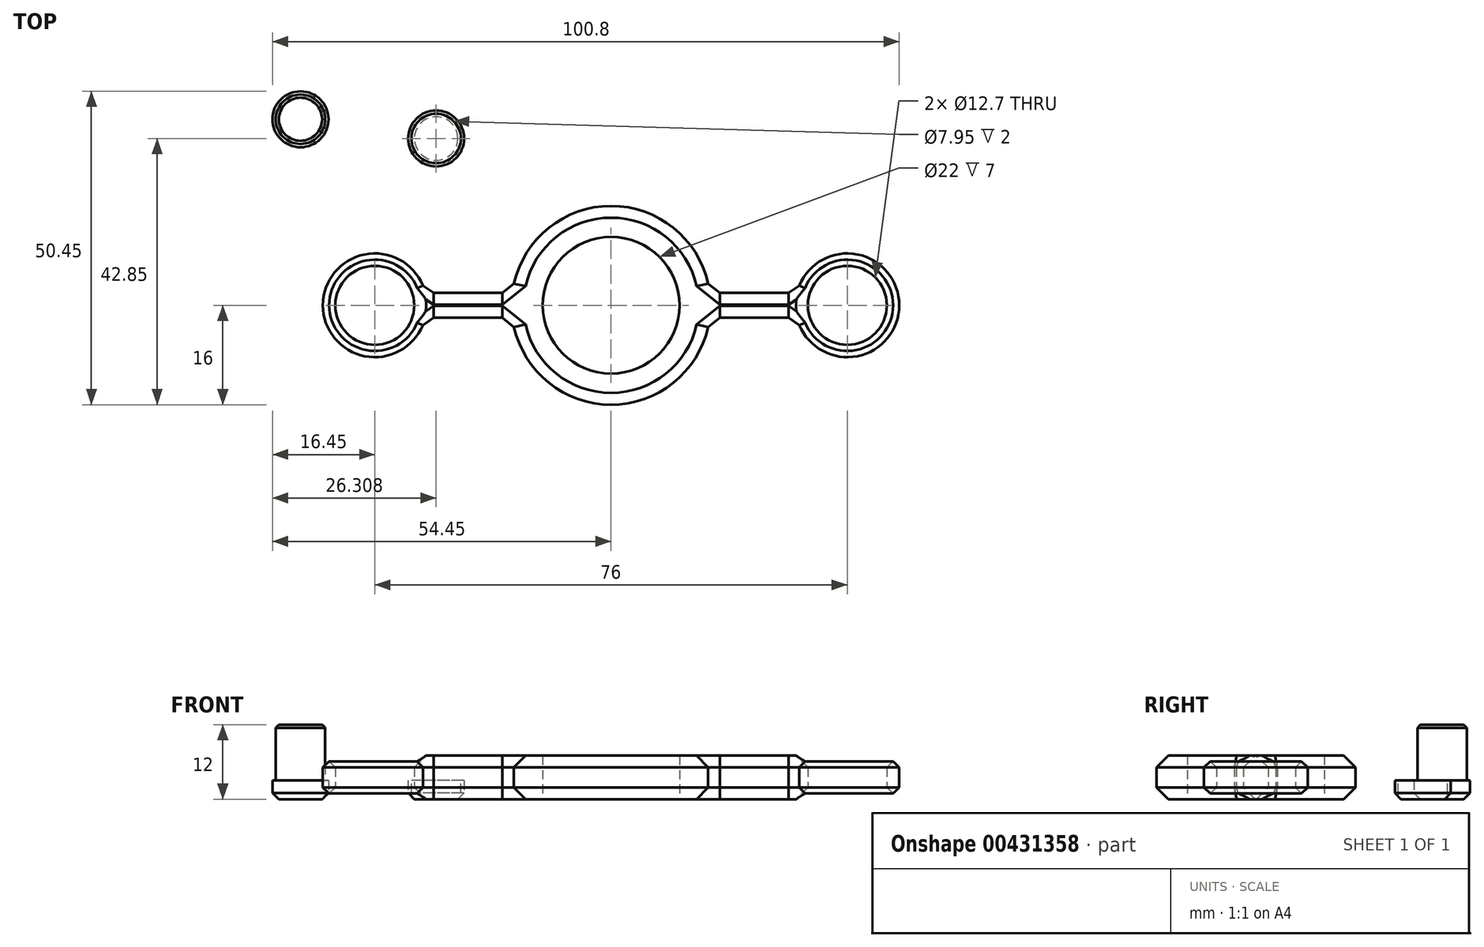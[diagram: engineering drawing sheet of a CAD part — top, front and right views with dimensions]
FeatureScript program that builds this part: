
annotation { "Feature Type Name" : "Feature", "Feature Type Description" : "" }
export const myFeature = defineFeature(function(context is Context, id is Id, definition is map)
    precondition{}
    {
        {
            var Q0;
            Q0=qCreatedBy(makeId("Top.planeOp"),FACE);
            var sketch = newSketch(context, id + "F0", { "sketchPlane" : qUnion([Q0])});
            skCircle(sketch, "E0", {"center": v(0, 0) * mm, "radius": 11 * mm});
            skArc(sketch, "E1.0", {"start": v(15.87, 2) * mm, "mid": v(0, 16) * mm, "end": v(-15.87, 2) * mm});
            skCircle(sketch, "E2", {"center": v(38, 0) * mm, "radius": 6.35 * mm});
            skArc(sketch, "E3.0", {"start": v(29.9, -2) * mm, "mid": v(46.35, 0) * mm, "end": v(29.9, 2) * mm});
            skLineSegment(sketch, "E4.trimOffspring", {"start": v(15.87, 2) * mm, "end": v(29.9, 2) * mm});
            skLineSegment(sketch, "E5.trimOffspring", {"start": v(15.87, -2) * mm, "end": v(29.9, -2) * mm});
            skArc(sketch, "E6.MirrorCS", {"start": v(-29.9, -2) * mm, "mid": v(-46.35, 0) * mm, "end": v(-29.9, 2) * mm});
            skLineSegment(sketch, "E7.MirrorCS", {"start": v(-15.87, 2) * mm, "end": v(-29.9, 2) * mm});
            skLineSegment(sketch, "E8.MirrorCS", {"start": v(-15.87, -2) * mm, "end": v(-29.9, -2) * mm});
            skCircle(sketch, "E9.MirrorC", {"center": v(-38, 0) * mm, "radius": 6.35 * mm});
            skArc(sketch, "E10.MirrorCS", {"start": v(-15.87, 2) * mm, "mid": v(0, 16) * mm, "end": v(15.87, 2) * mm});
            skArc(sketch, "E11.trimOffspring", {"start": v(15.87, -2) * mm, "mid": v(0, -16) * mm, "end": v(-15.87, -2) * mm});
            skArc(sketch, "E12.trimOffspring", {"start": v(-15.87, -2) * mm, "mid": v(0, -16) * mm, "end": v(15.87, -2) * mm});
            skSolve(sketch);
        }
        {
            var Q0;
            Q0=makeQuery(id+"F0.imprint","IMPRINT",FACE,{"disambiguationData":[TD([[makeQuery(id+"F0.imprint","IMPRINT",EDGE,{"derivedFrom":sQuery(id+"F0.wireOp",EDGE,"E2")}),-1.0]])]});
            extrude(context, id + "F1", {"entities" : qUnion([Q0]), "depth" : 7 * mm});
        }
        {
            var Q0;
            Q0=makeQuery(id+"F1.opExtrude","CAP_EDGE",EDGE,{"disambiguationData":[OSD([sQuery(id+"F0.wireOp",EDGE,"E12.trimOffspring")])],"isStart":false});
            var Q1;
            Q1=makeQuery(id+"F1.opExtrude","CAP_EDGE",EDGE,{"disambiguationData":[OSD([sQuery(id+"F0.wireOp",EDGE,"E5.trimOffspring")])],"isStart":false});
            var Q2;
            Q2=makeQuery(id+"F1.opExtrude","CAP_EDGE",EDGE,{"disambiguationData":[OSD([sQuery(id+"F0.wireOp",EDGE,"E3.0")])],"isStart":false});
            var Q3;
            Q3=makeQuery(id+"F1.opExtrude","CAP_EDGE",EDGE,{"disambiguationData":[OSD([sQuery(id+"F0.wireOp",EDGE,"E4.trimOffspring")])],"isStart":false});
            var Q4;
            Q4=makeQuery(id+"F1.opExtrude","CAP_EDGE",EDGE,{"disambiguationData":[OSD([sQuery(id+"F0.wireOp",EDGE,"E10.MirrorCS")])],"isStart":false});
            var Q5;
            Q5=makeQuery(id+"F1.opExtrude","CAP_EDGE",EDGE,{"disambiguationData":[OSD([sQuery(id+"F0.wireOp",EDGE,"E7.MirrorCS")])],"isStart":false});
            var Q6;
            Q6=makeQuery(id+"F1.opExtrude","CAP_EDGE",EDGE,{"disambiguationData":[OSD([sQuery(id+"F0.wireOp",EDGE,"E8.MirrorCS")])],"isStart":false});
            var Q7;
            Q7=makeQuery(id+"F1.opExtrude","CAP_EDGE",EDGE,{"disambiguationData":[OSD([sQuery(id+"F0.wireOp",EDGE,"E6.MirrorCS")])],"isStart":false});
            var Q8;
            Q8=makeQuery(id+"F1.opExtrude","CAP_EDGE",EDGE,{"disambiguationData":[OSD([sQuery(id+"F0.wireOp",EDGE,"E12.trimOffspring")])],"isStart":true});
            var Q9;
            Q9=makeQuery(id+"F1.opExtrude","CAP_EDGE",EDGE,{"disambiguationData":[OSD([sQuery(id+"F0.wireOp",EDGE,"E8.MirrorCS")])],"isStart":true});
            var Q10;
            Q10=makeQuery(id+"F1.opExtrude","CAP_EDGE",EDGE,{"disambiguationData":[OSD([sQuery(id+"F0.wireOp",EDGE,"E6.MirrorCS")])],"isStart":true});
            var Q11;
            Q11=makeQuery(id+"F1.opExtrude","CAP_EDGE",EDGE,{"disambiguationData":[OSD([sQuery(id+"F0.wireOp",EDGE,"E7.MirrorCS")])],"isStart":true});
            var Q12;
            Q12=makeQuery(id+"F1.opExtrude","CAP_EDGE",EDGE,{"disambiguationData":[OSD([sQuery(id+"F0.wireOp",EDGE,"E10.MirrorCS")])],"isStart":true});
            var Q13;
            Q13=makeQuery(id+"F1.opExtrude","CAP_EDGE",EDGE,{"disambiguationData":[OSD([sQuery(id+"F0.wireOp",EDGE,"E4.trimOffspring")])],"isStart":true});
            var Q14;
            Q14=makeQuery(id+"F1.opExtrude","CAP_EDGE",EDGE,{"disambiguationData":[OSD([sQuery(id+"F0.wireOp",EDGE,"E3.0")])],"isStart":true});
            var Q15;
            Q15=makeQuery(id+"F1.opExtrude","CAP_EDGE",EDGE,{"disambiguationData":[OSD([sQuery(id+"F0.wireOp",EDGE,"E5.trimOffspring")])],"isStart":true});
            var Q16;
            Q16=makeQuery(id+"F1.opExtrude","SWEPT_FACE",FACE,{"disambiguationData":[OSD([sQuery(id+"F0.wireOp",EDGE,"E5.trimOffspring")])]});
            var Q17;
            Q17=makeQuery(id+"F1.opExtrude","SWEPT_FACE",FACE,{"disambiguationData":[OSD([sQuery(id+"F0.wireOp",EDGE,"E4.trimOffspring")])]});
            var Q18;
            Q18=makeQuery(id+"F1.opExtrude","SWEPT_FACE",FACE,{"disambiguationData":[OSD([sQuery(id+"F0.wireOp",EDGE,"E7.MirrorCS")])]});
            var Q19;
            Q19=makeQuery(id+"F1.opExtrude","SWEPT_FACE",FACE,{"disambiguationData":[OSD([sQuery(id+"F0.wireOp",EDGE,"E8.MirrorCS")])]});
            var Q20;
            Q20=makeQuery(id+"F1.opExtrude","SWEPT_FACE",FACE,{"disambiguationData":[OSD([sQuery(id+"F0.wireOp",EDGE,"E2")])]});
            var Q21;
            Q21=makeQuery(id+"F1.opExtrude","SWEPT_FACE",FACE,{"disambiguationData":[OSD([sQuery(id+"F0.wireOp",EDGE,"E9.MirrorC")])]});
            chamfer(context, id + "F2", {"entities" : qUnion([Q0, Q1, Q2, Q3, Q4, Q5, Q6, Q7, Q8, Q9, Q10, Q11, Q12, Q13, Q14, Q15, Q16, Q17, Q18, Q19, Q20, Q21]), "width" : 1.9 * mm, "tangentPropagation" : true});
        }
        {
            var Q0;
            Q0=qCreatedBy(makeId("Top.planeOp"),FACE);
            var sketch = newSketch(context, id + "F3", { "sketchPlane" : qUnion([Q0])});
            skCircle(sketch, "E13", {"center": v(-49.95, 29.95) * mm, "radius": 4.5 * mm});
            skSolve(sketch);
        }
        {
            var Q0;
            Q0=makeQuery(id+"F3.imprint","IMPRINT",FACE,{"disambiguationData":[TD([[makeQuery(id+"F3.imprint","IMPRINT",EDGE,{"derivedFrom":sQuery(id+"F3.wireOp",EDGE,"E13")}),1.0]])]});
            extrude(context, id + "F4", {"entities" : qUnion([Q0]), "depth" : 3 * mm});
        }
        {
            var Q0;
            Q0=makeQuery(id+"F4.opExtrude","CAP_FACE",FACE,{"disambiguationData":[OSD([sQuery(id+"F3.wireOp",EDGE,"E13")])],"isStart":false});
            var sketch = newSketch(context, id + "F5", { "sketchPlane" : qUnion([Q0])});
            skCircle(sketch, "E14", {"center": v(-49.95, 29.95) * mm, "radius": 3.98 * mm});
            skSolve(sketch);
        }
        {
            var Q0;
            Q0=makeQuery(id+"F5.imprint","IMPRINT",FACE,{"disambiguationData":[TD([[makeQuery(id+"F5.imprint","IMPRINT",EDGE,{"derivedFrom":sQuery(id+"F5.wireOp",EDGE,"E14")}),1.0]])]});
            extrude(context, id + "F6", {"entities" : qUnion([Q0]), "operationType" : NewBodyOperationType.ADD, "depth" : 9 * mm});
        }
        {
            var Q0;
            Q0=makeQuery(id+"F6.opExtrude","CAP_EDGE",EDGE,{"disambiguationData":[OSD([sQuery(id+"F5.wireOp",EDGE,"E14")])],"isStart":false});
            chamfer(context, id + "F7", {"entities" : qUnion([Q0]), "width" : .5 * mm, "tangentPropagation" : true});
        }
        {
            var Q0;
            Q0=makeQuery(id+"F4.opExtrude","CAP_EDGE",EDGE,{"disambiguationData":[OSD([sQuery(id+"F3.wireOp",EDGE,"E13")])],"isStart":true});
            chamfer(context, id + "F8", {"entities" : qUnion([Q0]), "width" : 1 * mm, "tangentPropagation" : true});
        }
        {
            var Q0;
            Q0=qCreatedBy(makeId("Top.planeOp"),FACE);
            var sketch = newSketch(context, id + "F9", { "sketchPlane" : qUnion([Q0])});
            skCircle(sketch, "E15", {"center": v(-28.14, 26.85) * mm, "radius": 4.5 * mm});
            skSolve(sketch);
        }
        {
            var Q0;
            Q0=makeQuery(id+"F9.imprint","IMPRINT",FACE,{"disambiguationData":[TD([[makeQuery(id+"F9.imprint","IMPRINT",EDGE,{"derivedFrom":sQuery(id+"F9.wireOp",EDGE,"E15")}),1.0]])]});
            extrude(context, id + "F10", {"entities" : qUnion([Q0]), "depth" : 3 * mm});
        }
        {
            var Q0;
            Q0=makeQuery(id+"F10.opExtrude","CAP_FACE",FACE,{"disambiguationData":[OSD([sQuery(id+"F9.wireOp",EDGE,"E15")])],"isStart":false});
            var sketch = newSketch(context, id + "F11", { "sketchPlane" : qUnion([Q0])});
            skCircle(sketch, "E16", {"center": v(-28.14, 26.85) * mm, "radius": 3.98 * mm});
            skSolve(sketch);
        }
        {
            var Q0;
            Q0=makeQuery(id+"F11.imprint","IMPRINT",FACE,{"disambiguationData":[TD([[makeQuery(id+"F11.imprint","IMPRINT",EDGE,{"derivedFrom":sQuery(id+"F11.wireOp",EDGE,"E16")}),1.0]])]});
            extrude(context, id + "F12", {"entities" : qUnion([Q0]), "operationType" : NewBodyOperationType.REMOVE, "oppositeDirection" : true, "depth" : 2 * mm});
        }
        {
            var Q0;
            Q0=makeQuery(id+"F10.opExtrude","CAP_EDGE",EDGE,{"disambiguationData":[OSD([sQuery(id+"F9.wireOp",EDGE,"E15")])],"isStart":true});
            chamfer(context, id + "F13", {"entities" : qUnion([Q0]), "width" : 1 * mm, "tangentPropagation" : true});
        }
    });
